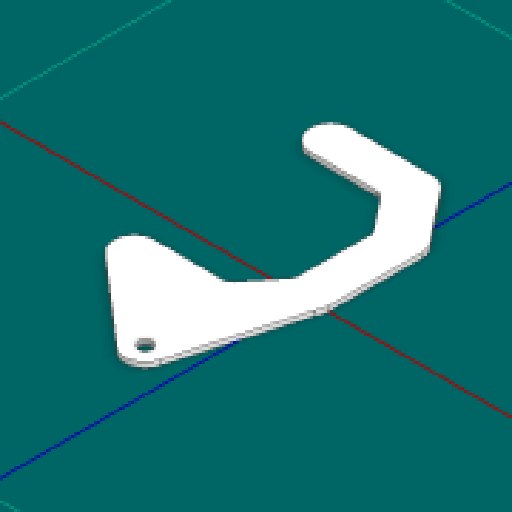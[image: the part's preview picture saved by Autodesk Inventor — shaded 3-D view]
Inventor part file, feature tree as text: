
AUTODESK INVENTOR PART (.ipt)
format: ipt  version: 2025 (Build 290162000, 162)  size: 168,960 bytes
history: native  units: in
note: dims shown in document units (in); Inventor stores cm internally (conversion verified against a paired STEP export)
features: other x8, extrude x1, sketch x1, reference x1
ambient origin geometry x8: Origin, YZ Plane, XZ Plane, XY Plane, X Axis, Y Axis, Z Axis, Center Point
bodies: Solid1 (feature_tree)
feature tree (11):
  other  "Blocks"
  extrude  "Extrusion1"  Depth=0.5in
  sketch  "Sketch1"  dims[d0=0.5in d1=0.5in d2=0.5in d3=0.125in d4=0.0625in d5=0.0in d6=0.176in d7=0.176in d8=0.176in d9=0.176in d10=0.5in d11=0.5in d12=0.25in d13=0.25in d14=0.625in d15=0.625in d16=0.5in d18=0.5in]
  other  "main_gusset"
  reference  "Reference2"
  other  "main_gusset:1"
  other  "<userpath>\vex_robotics_high_stakes\hardware\cad\ATLAS\chassis\drivetrain.iam"
  other  "drivetrain.iam"
  other  "!structure:1"
  other  "rail:1"
  other  "Alu Angle 1x1x12:1"
